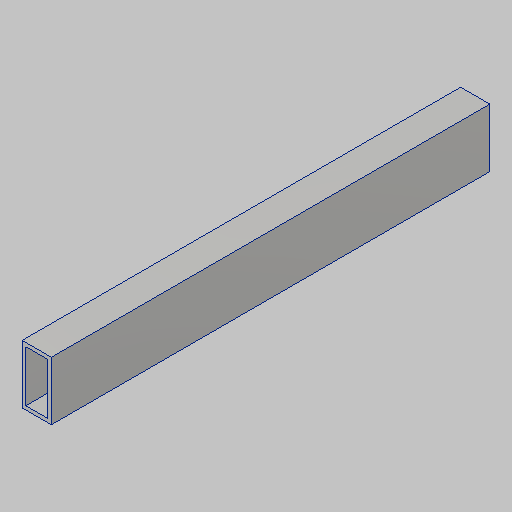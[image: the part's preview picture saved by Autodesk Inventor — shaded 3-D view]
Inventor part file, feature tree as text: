
AUTODESK INVENTOR PART (.ipt)
format: ipt  version: 2023.5 (Build 275446000, 446)  size: 170,496 bytes
history: native  units: in
note: dims shown in document units (in); Inventor stores cm internally (conversion verified against a paired STEP export)
features: extrude x1
ambient origin geometry x8: Origin, YZ Plane, XZ Plane, XY Plane, X Axis, Y Axis, Z Axis, Center Point
bodies: Solid1 (feature_tree)
feature tree (1):
  extrude  "Extrusion1"  TaperAngle=0.0deg  [1 undecoded]
note: 1 required parameter value undecoded (feature->parameter linkage not recoverable at this tier; creation-order binding heuristic only, values carry confidence <= 0.55)
